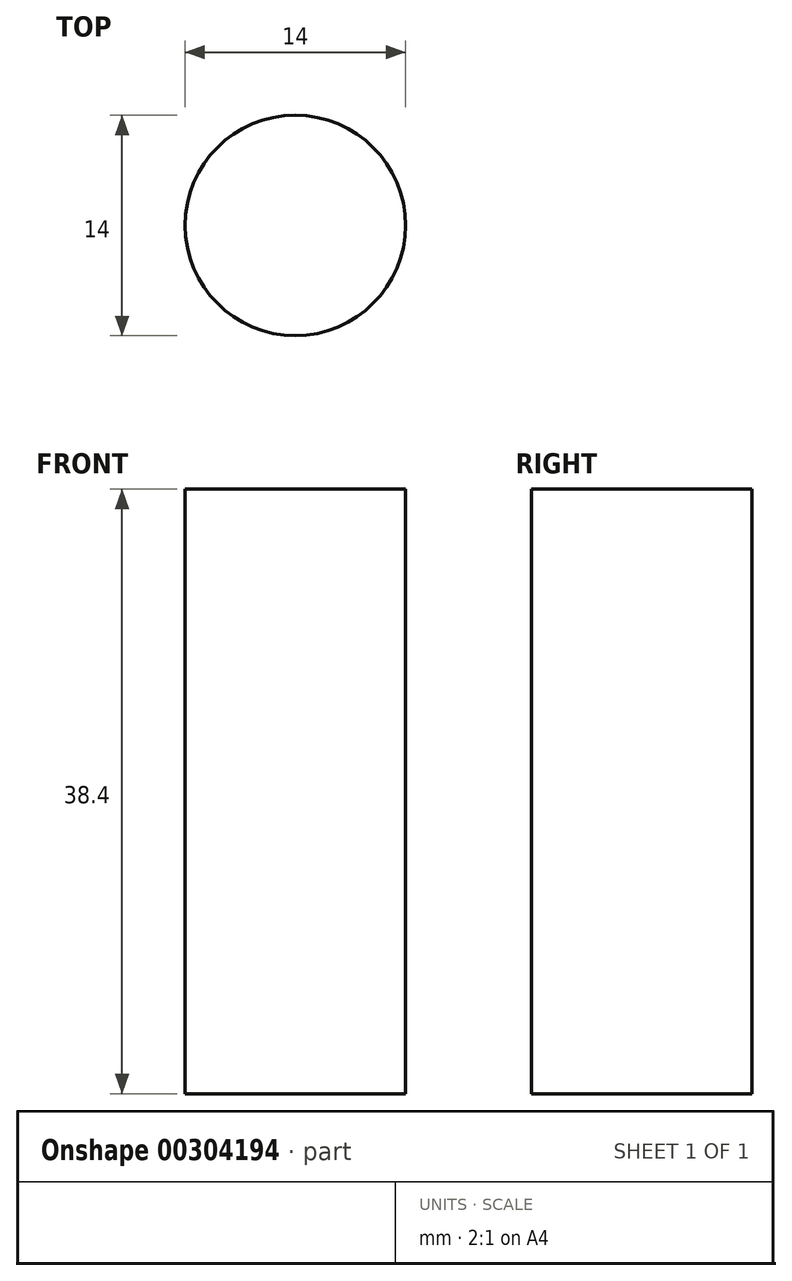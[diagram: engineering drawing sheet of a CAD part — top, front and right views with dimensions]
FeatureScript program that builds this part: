
annotation { "Feature Type Name" : "Feature", "Feature Type Description" : "" }
export const myFeature = defineFeature(function(context is Context, id is Id, definition is map)
    precondition{}
    {
        {
            var Q0;
            Q0=qCreatedBy(makeId("Top.planeOp"),FACE);
            var sketch = newSketch(context, id + "F0", { "sketchPlane" : qUnion([Q0])});
            skCircle(sketch, "E0", {"center": v(0, 0) * mm, "radius": 7 * mm});
            skSolve(sketch);
        }
        {
            var Q0;
            Q0 = qSketchRegion(id + "F0", true);
            extrude(context, id + "F1", {"entities" : qUnion([Q0]), "depth" : 38.4 * mm, "offsetDistance" : 25 * mm});
        }
    });
